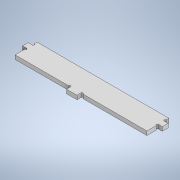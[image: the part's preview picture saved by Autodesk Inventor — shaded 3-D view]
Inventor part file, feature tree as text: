
AUTODESK INVENTOR PART (.ipt)
format: ipt  version: 2020 (Build 240168000, 168)  size: 141,824 bytes
history: native  units: mm
features: extrude x1, sketch x1
ambient origin geometry x8: Origin, YZ Plane, XZ Plane, XY Plane, X Axis, Y Axis, Z Axis, Center Point
bodies: Solid1 (feature_tree)
feature tree (2):
  extrude  "Extrusion1"  Depth=20.0mm
  sketch  "Sketch1"  dims[d2=3.5mm d5=3.5mm d9=7.0mm d11=10.0mm d24=7.0mm d25=0.0mm d32=5.0mm d33=230.666667mm d36=7.0mm d42=3.5mm d43=97.083333mm d44=3.5mm d45=18.25mm d46=20.0mm]
